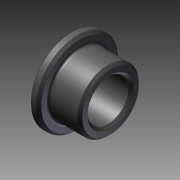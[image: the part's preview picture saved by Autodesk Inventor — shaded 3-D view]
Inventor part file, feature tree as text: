
AUTODESK INVENTOR PART (.ipt)
format: ipt  version: 2011 SP1 (Build 150282100, 282)  size: 116,736 bytes
history: native  units: mm
features: revolve x1, sketch x1
ambient origin geometry x8: Origin, YZ Plane, XZ Plane, XY Plane, X Axis, Y Axis, Z Axis, Center Point
bodies: Solid1 (feature_tree)
feature tree (2):
  revolve  "Revolution1"  [1 undecoded]
  sketch  "Skizze_1"  dims[d0=360.0deg]
note: 1 required parameter value undecoded (feature->parameter linkage not recoverable at this tier; creation-order binding heuristic only, values carry confidence <= 0.55)
